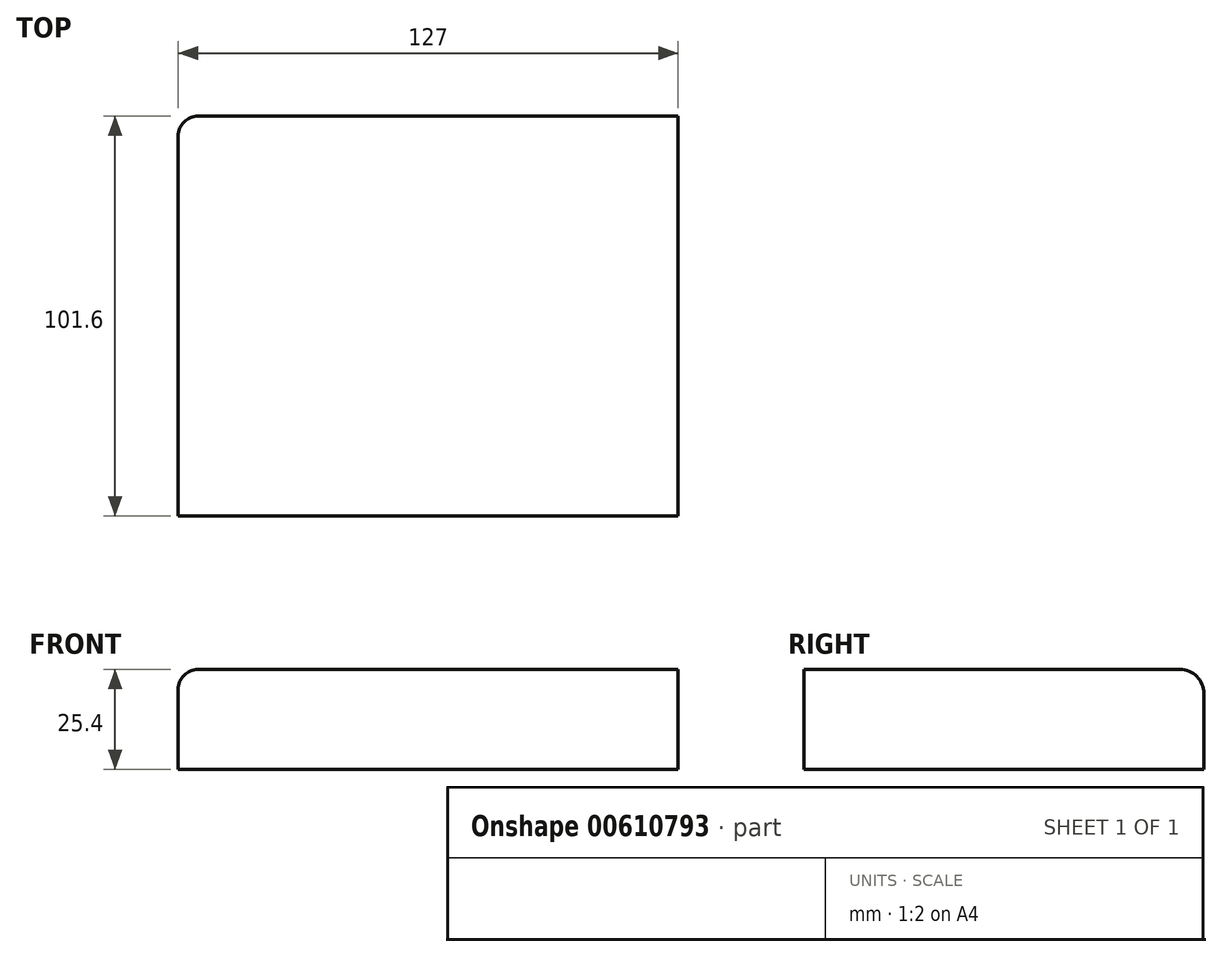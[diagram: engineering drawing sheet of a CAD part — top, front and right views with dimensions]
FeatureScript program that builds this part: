
annotation { "Feature Type Name" : "Feature", "Feature Type Description" : "" }
export const myFeature = defineFeature(function(context is Context, id is Id, definition is map)
    precondition{}
    {
        {
            var Q0;
            Q0=qCreatedBy(makeId("Top.planeOp"),FACE);
            var sketch = newSketch(context, id + "F0", { "sketchPlane" : qUnion([Q0])});
            skLineSegment(sketch, "E0.bottom", {"start": v(-63.5, 50.8) * mm, "end": v(63.5, 50.8) * mm});
            skLineSegment(sketch, "E0.top", {"start": v(-63.5, -50.8) * mm, "end": v(63.5, -50.8) * mm});
            skLineSegment(sketch, "E0.left", {"start": v(-63.5, 50.8) * mm, "end": v(-63.5, -50.8) * mm});
            skLineSegment(sketch, "E0.right", {"start": v(63.5, 50.8) * mm, "end": v(63.5, -50.8) * mm});
            skPoint(sketch, "E0.middle", {"position": v(0, 0) * mm});
            skSolve(sketch);
        }
        {
            var Q0;
            Q0 = qSketchRegion(id + "F0", true);
            extrude(context, id + "F1", {"entities" : qUnion([Q0]), "depth" : 25.4 * mm, "offsetDistance" : 25.4 * mm});
        }
        {
            var Q0;
            Q0=makeQuery(id+"F1.opExtrude","CAP_EDGE",EDGE,{"disambiguationData":[OSD([sQuery(id+"F0.wireOp",EDGE,"E0.bottom")])],"isStart":false});
            fillet(context, id + "F2", {"entities" : qUnion([Q0]), "radius" : 6.13 * mm, "tangentPropagation" : true, "allowEdgeOverflow" : false});
        }
        {
            var Q0;
            Q0=makeQuery(id+"F1.opExtrude","CAP_EDGE",EDGE,{"disambiguationData":[OSD([sQuery(id+"F0.wireOp",EDGE,"E0.left")])],"isStart":false});
            fillet(context, id + "F3", {"entities" : qUnion([Q0]), "radius" : 5.08 * mm, "tangentPropagation" : true, "allowEdgeOverflow" : false});
        }
    });
